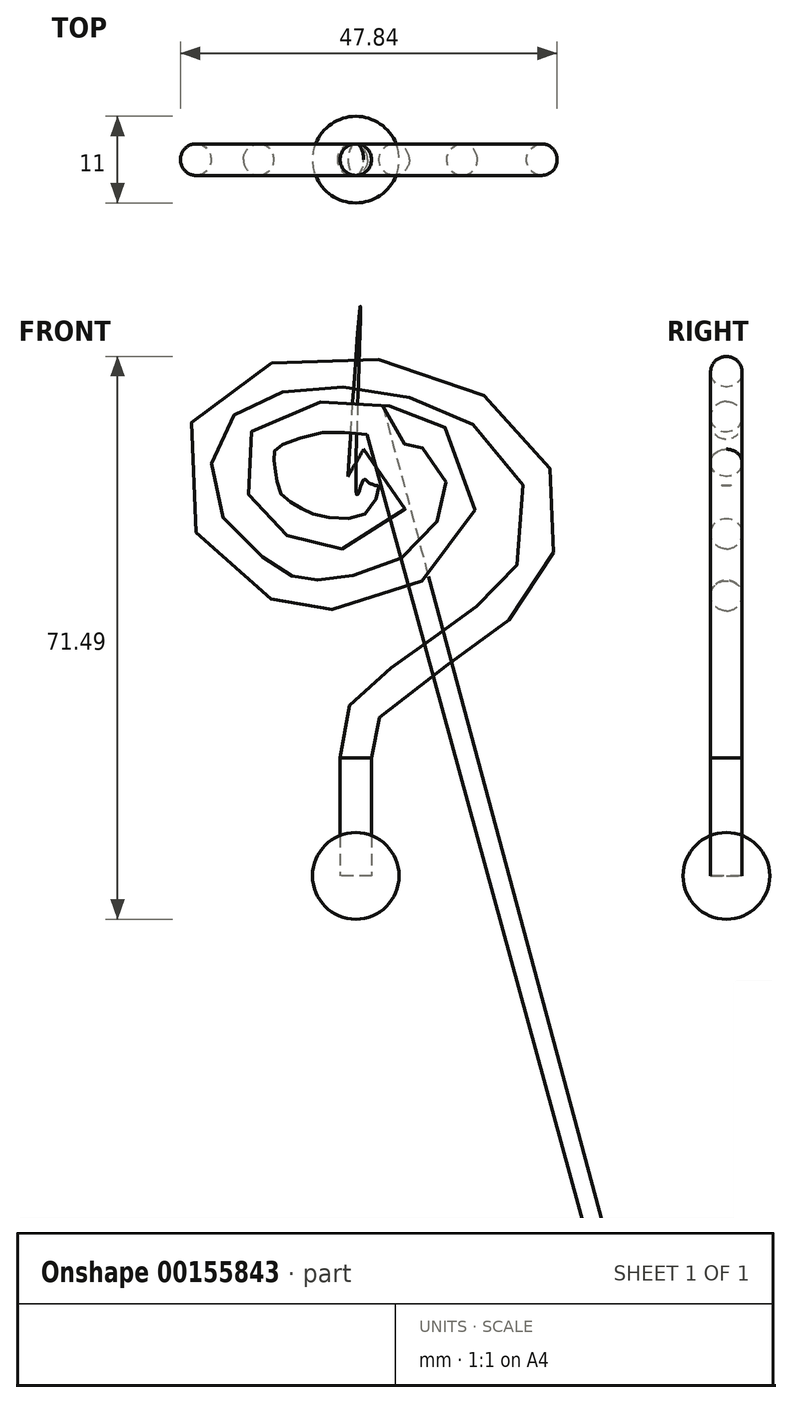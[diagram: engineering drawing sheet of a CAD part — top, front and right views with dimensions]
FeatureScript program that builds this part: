
annotation { "Feature Type Name" : "Feature", "Feature Type Description" : "" }
export const myFeature = defineFeature(function(context is Context, id is Id, definition is map)
    precondition{}
    {
        {
            var Q0;
            Q0=qCreatedBy(makeId("Top.planeOp"),FACE);
            var sketch = newSketch(context, id + "F0", { "sketchPlane" : qUnion([Q0])});
            skArc(sketch, "E0", {"start": v(-48.64, 0.62) * mm, "mid": v(-54.14, -4.88) * mm, "end": v(-48.64, -10.38) * mm});
            skLineSegment(sketch, "E1", {"start": v(-48.64, 0.62) * mm, "end": v(-48.64, -10.38) * mm});
            skSolve(sketch);
        }
        {
            var Q0;
            Q0=makeQuery(id+"F0.imprint","IMPRINT",FACE,{"disambiguationData":[TD([[makeQuery(id+"F0.imprint","IMPRINT",EDGE,{"derivedFrom":sQuery(id+"F0.wireOp",EDGE,"E0")}),1.0]])]});
            var Q1;
            Q1=sQuery(id+"F0.wireOp",EDGE,"E1");
            revolve(context, id + "F1", {"entities" : qUnion([Q0]), "axis" : qUnion([Q1]), "revolveType" : RevolveType.FULL});
        }
        {
            var Q0;
            Q0=qCreatedBy(makeId("Top.planeOp"),FACE);
            var sketch = newSketch(context, id + "F2", { "sketchPlane" : qUnion([Q0])});
            skPoint(sketch, "E2.0", {"position": v(-48.64, -4.88) * mm});
            skCircle(sketch, "E3", {"center": v(-48.64, -4.88) * mm, "radius": 2 * mm});
            skSolve(sketch);
        }
        {
            var Q0;
            Q0=makeQuery(id+"F2.imprint","IMPRINT",FACE,{"disambiguationData":[TD([[makeQuery(id+"F2.imprint","IMPRINT",EDGE,{"derivedFrom":sQuery(id+"F2.wireOp",EDGE,"E3")}),1.0]])]});
            extrude(context, id + "F3", {"entities" : qUnion([Q0]), "depth" : 15 * mm});
        }
        {
            var Q0;
            Q0=qCreatedBy(makeId("Front.planeOp"),FACE);
            var sketch = newSketch(context, id + "F4", { "sketchPlane" : qUnion([Q0])});
            skLineSegment(sketch, "E4.0", {"start": v(-50.64, 15) * mm, "end": v(-46.64, 15) * mm});
            skPoint(sketch, "E5.1.internal.snap0", {"position": v(-48.64, 15) * mm});
            skPoint(sketch, "E5.28.internal.snap0", {"position": v(-48.64, 15) * mm});
            skFitSpline(sketch, "E5", {"points": [v(-48.64, 15) * mm, v(-48.64, 19.2) * mm, v(-41.1, 26.21) * mm, v(-33.36, 31.78) * mm, v(-26.95, 37.7) * mm, v(-25.01, 45.33) * mm, v(-27.43, 54.29) * mm, v(-39.66, 62.15) * mm, v(-56.23, 63.72) * mm, v(-66.88, 58.28) * mm, v(-67.36, 44.85) * mm, v(-57.68, 36.38) * mm, v(-55.75, 35.65) * mm, v(-46.07, 36.86) * mm, v(-37.72, 42.43) * mm, v(-35.42, 50.78) * mm, v(-40.14, 56.83) * mm, v(-41.95, 57.43) * mm, v(-50.64, 58.28) * mm, v(-54.05, 58.04) * mm, v(-60.22, 55.38) * mm, v(-60.83, 51.62) * mm, v(-59.98, 47.87) * mm, v(-58.05, 45.94) * mm, v(-54.3, 44) * mm, v(-50.64, 43.52) * mm, v(-46.43, 44.36) * mm, v(-43.89, 49.69) * mm, v(-48.64, 52.47) * mm], "startDerivative": vector(-36.43, 148.45) * mm, "endDerivative": vector(-205.36, 58.96) * mm});
            skSolve(sketch);
        }
        {
            var Q0;
            Q0=makeQuery(id+"F3.opExtrude","CAP_FACE",FACE,{"disambiguationData":[OSD([sQuery(id+"F2.wireOp",EDGE,"E3")])],"isStart":false});
            var Q1;
            Q1=sQuery(id+"F4.wireOp",EDGE,"E5");
            sweep(context, id + "F5", {"operationType" : NewBodyOperationType.ADD, "profiles" : qUnion([Q0]), "path" : qUnion([Q1])});
        }
    });
